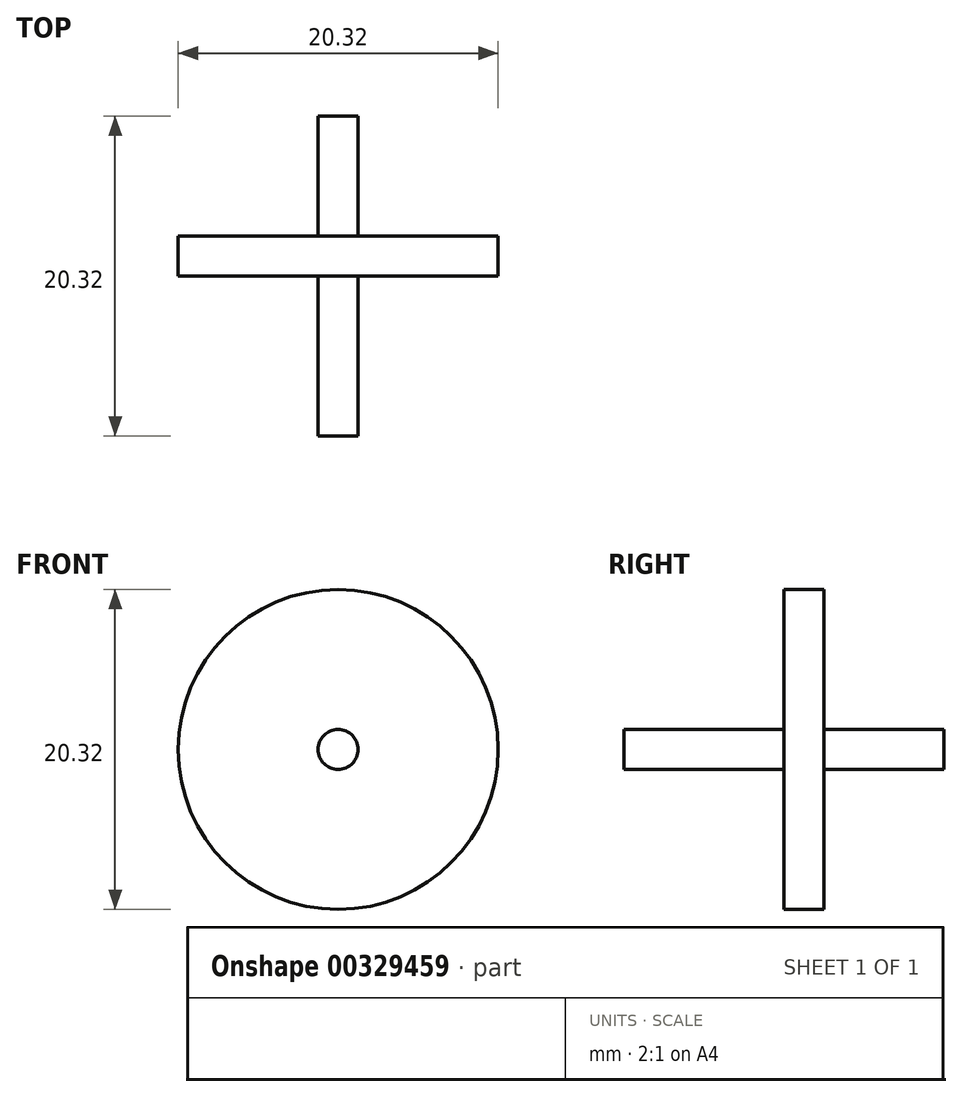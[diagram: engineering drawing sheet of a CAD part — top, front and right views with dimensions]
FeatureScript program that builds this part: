
annotation { "Feature Type Name" : "Feature", "Feature Type Description" : "" }
export const myFeature = defineFeature(function(context is Context, id is Id, definition is map)
    precondition{}
    {
        {
            var Q0;
            Q0=qCreatedBy(makeId("Front.planeOp"),FACE);
            var sketch = newSketch(context, id + "F0", { "sketchPlane" : qUnion([Q0])});
            skCircle(sketch, "E0", {"center": v(0, 0) * mm, "radius": 1.27 * mm});
            skSolve(sketch);
        }
        {
            var Q0;
            Q0=qSketchRegion(id+"F0",true);
            extrude(context, id + "F1", {"entities" : qUnion([Q0]), "depth" : 20.32 * mm});
        }
        {
            var Q0;
            Q0=makeQuery(id+"F1.opExtrude","CAP_FACE",FACE,{"disambiguationData":[OSD([sQuery(id+"F0.wireOp",EDGE,"E0")])],"isStart":false});
            cPlane(context, id + "F2", {"entities" : qUnion([Q0]), "cplaneType" : CPlaneType.OFFSET, "offset" : 10.16 * mm, "oppositeDirection" : true, "width" : 152.4 * mm, "height" : 152.4 * mm});
        }
        {
            var Q0;
            Q0=qCreatedBy(id+"F2.planeOp",FACE);
            var sketch = newSketch(context, id + "F3", { "sketchPlane" : qUnion([Q0])});
            skCircle(sketch, "E1", {"center": v(0, 0) * mm, "radius": 10.16 * mm});
            skSolve(sketch);
        }
        {
            var Q0;
            Q0 = qSketchRegion(id + "F3", true);
            extrude(context, id + "F4", {"entities" : qUnion([Q0]), "operationType" : NewBodyOperationType.ADD, "oppositeDirection" : true, "depth" : 2.54 * mm});
        }
    });
